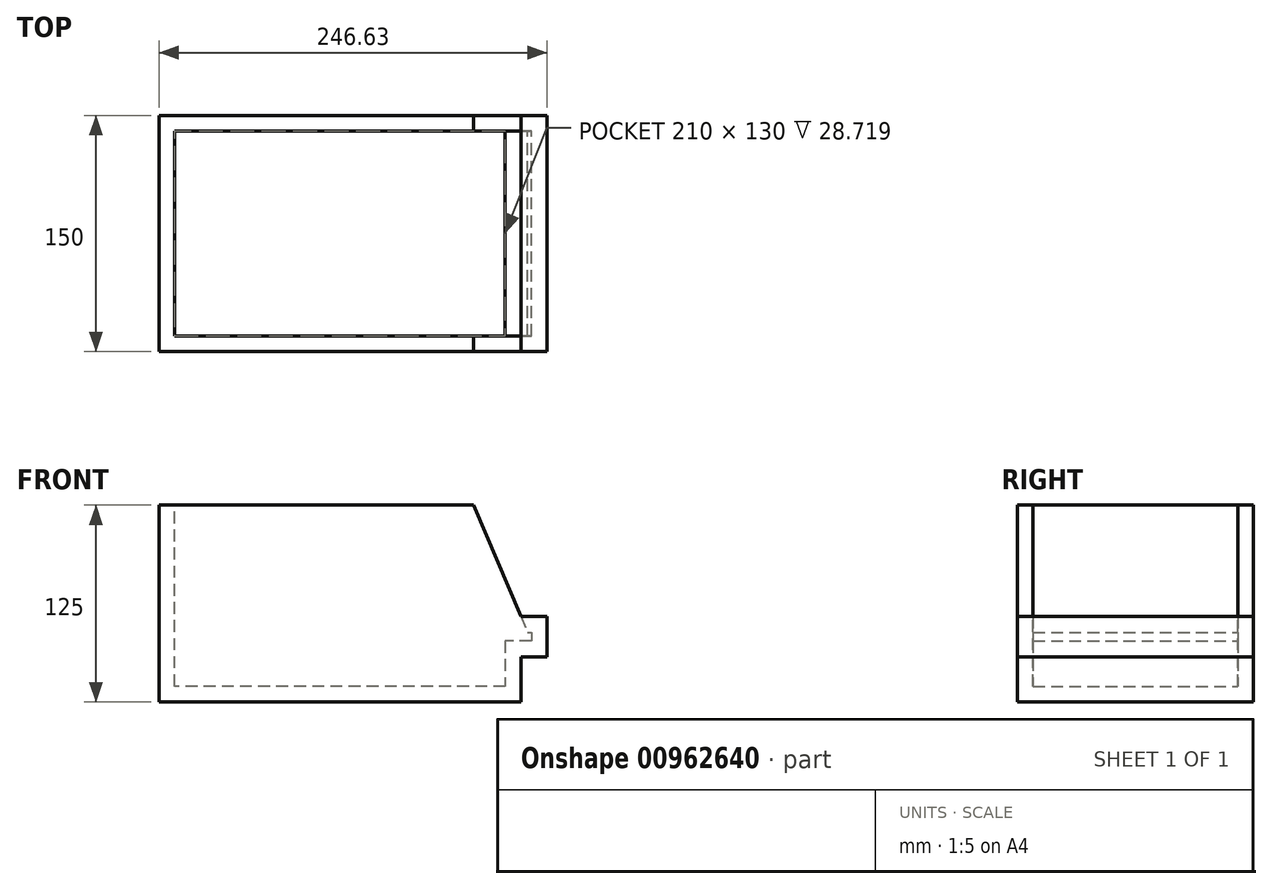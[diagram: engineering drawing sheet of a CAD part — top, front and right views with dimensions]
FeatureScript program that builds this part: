
annotation { "Feature Type Name" : "Feature", "Feature Type Description" : "" }
export const myFeature = defineFeature(function(context is Context, id is Id, definition is map)
    precondition{}
    {
        {
            var Q0;
            Q0=qCreatedBy(makeId("Front.planeOp"),FACE);
            var sketch = newSketch(context, id + "F0", { "sketchPlane" : qUnion([Q0])});
            skLineSegment(sketch, "E0", {"start": v(0, 0) * mm, "end": v(0, 125) * mm});
            skLineSegment(sketch, "E1", {"start": v(0, 125) * mm, "end": v(200, 125) * mm});
            skLineSegment(sketch, "E2", {"start": v(200, 125) * mm, "end": v(230, 54.28) * mm});
            skLineSegment(sketch, "E3", {"start": v(230, 54.28) * mm, "end": v(246.63, 54.28) * mm});
            skLineSegment(sketch, "E4", {"start": v(246.63, 54.28) * mm, "end": v(246.63, 28.72) * mm});
            skLineSegment(sketch, "E5", {"start": v(246.63, 28.72) * mm, "end": v(230, 28.72) * mm});
            skLineSegment(sketch, "E6", {"start": v(230, 28.72) * mm, "end": v(230, 0) * mm});
            skLineSegment(sketch, "E7", {"start": v(230, 0) * mm, "end": v(0, 0) * mm});
            skSolve(sketch);
        }
        {
            var Q0;
            Q0=makeQuery(id+"F0.imprint","IMPRINT",FACE,{"disambiguationData":[TD([[makeQuery(id+"F0.imprint","IMPRINT",EDGE,{"derivedFrom":sQuery(id+"F0.wireOp",EDGE,"E0")}),-1.0]])]});
            extrude(context, id + "F1", {"entities" : qUnion([Q0]), "depth" : 150 * mm, "offsetDistance" : 25 * mm});
        }
        {
            var Q0;
            Q0=makeQuery(id+"F1.opExtrude","SWEPT_FACE",FACE,{"disambiguationData":[OSD([sQuery(id+"F0.wireOp",EDGE,"E1")])]});
            var Q1;
            Q1=makeQuery(id+"F1.opExtrude","SWEPT_FACE",FACE,{"disambiguationData":[OSD([sQuery(id+"F0.wireOp",EDGE,"E2")])]});
            shell(context, id + "F2", {"entities" : qUnion([Q0, Q1]), "thickness" : 10 * mm});
        }
    });
